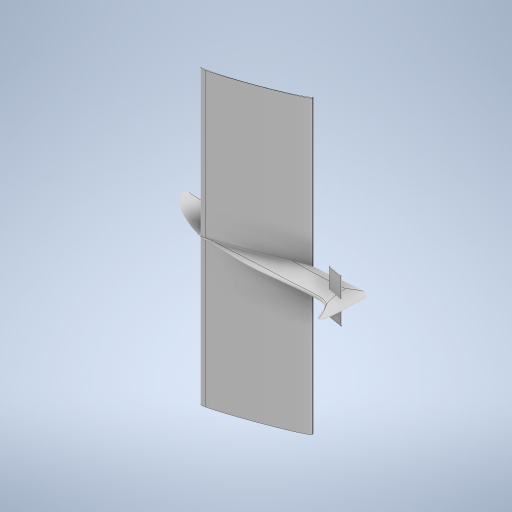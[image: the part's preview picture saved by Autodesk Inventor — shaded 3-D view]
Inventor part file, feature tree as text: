
AUTODESK INVENTOR PART (.ipt)
format: ipt  version: 2024 (Build 280153000, 153)  size: 699,392 bytes
history: native  units: mm
features: other x3, extrude x2, fillet x1
ambient origin geometry x8: Origin, YZ Plane, XZ Plane, XY Plane, X Axis, Y Axis, Z Axis, Center Point
bodies: Body1 (feature_tree), Body2 (feature_tree)
feature tree (6):
  other  "ソリッド1"
  extrude  "押し出し1"  Depth=1.047198mm TaperAngle=0.0deg
  extrude  "押し出し2"  Depth=150.0mm TaperAngle=0.0deg
  other  "フォーム2"
  fillet  "フィレット11"  Radius=3.490659mm
  other  "ソリッド2"
